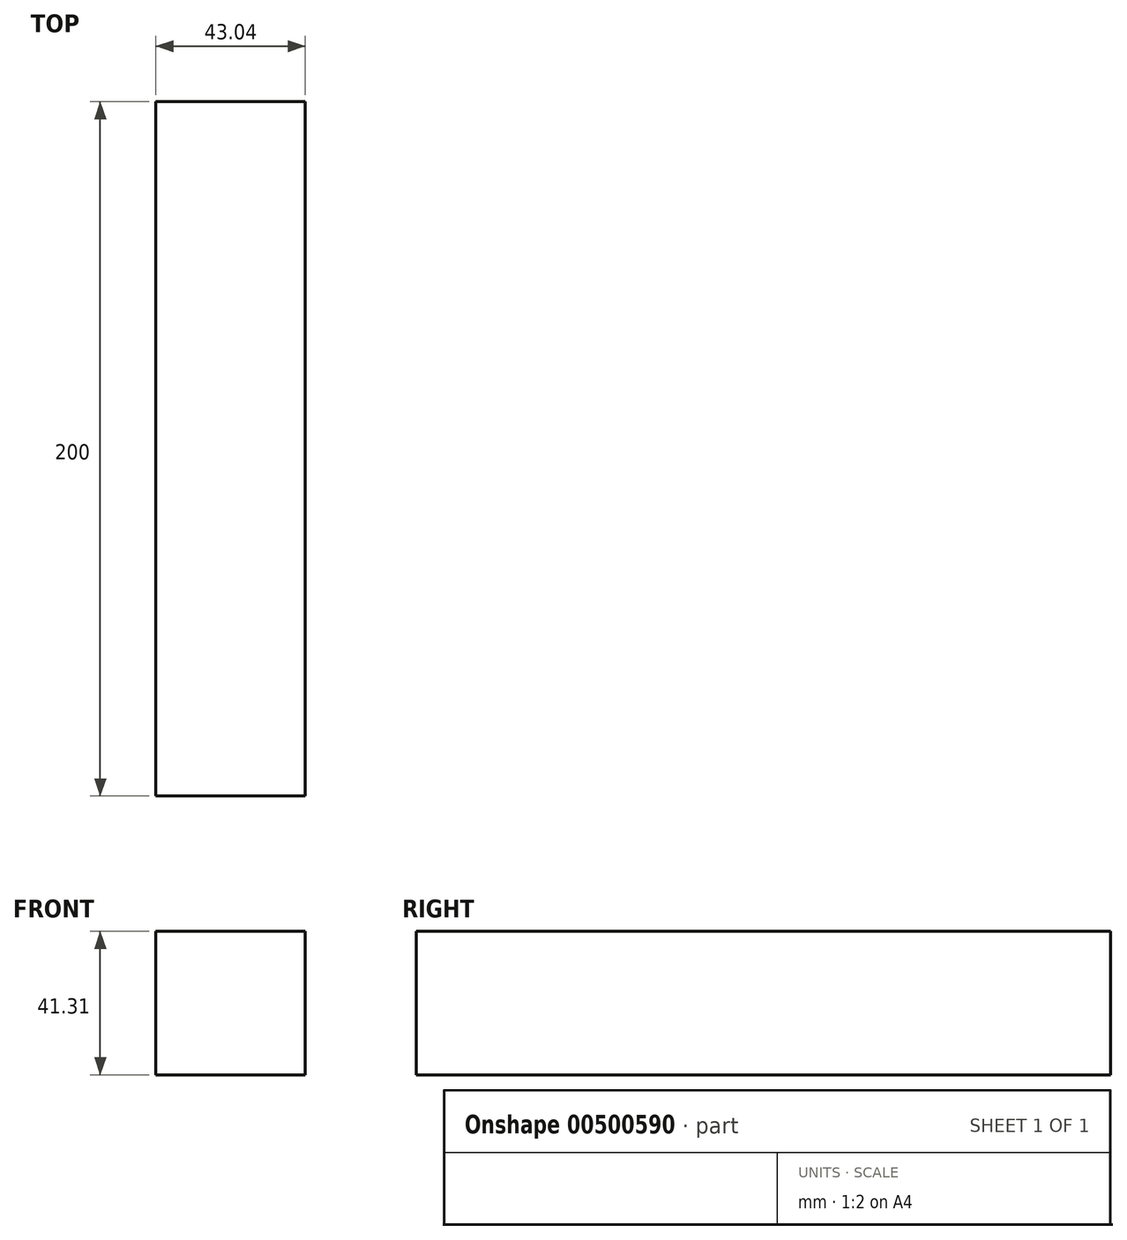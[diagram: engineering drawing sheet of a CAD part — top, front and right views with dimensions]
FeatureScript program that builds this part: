
annotation { "Feature Type Name" : "Feature", "Feature Type Description" : "" }
export const myFeature = defineFeature(function(context is Context, id is Id, definition is map)
    precondition{}
    {
        {
            var Q0;
            Q0=qCreatedBy(makeId("Front.planeOp"),FACE);
            var sketch = newSketch(context, id + "F0", { "sketchPlane" : qUnion([Q0])});
            skLineSegment(sketch, "E0.bottom", {"start": v(21.52, -23.38) * mm, "end": v(-21.52, -23.38) * mm});
            skLineSegment(sketch, "E0.top", {"start": v(21.52, 17.93) * mm, "end": v(-21.52, 17.93) * mm});
            skLineSegment(sketch, "E0.left", {"start": v(21.52, -23.38) * mm, "end": v(21.52, 17.93) * mm});
            skLineSegment(sketch, "E0.right", {"start": v(-21.52, -23.38) * mm, "end": v(-21.52, 17.93) * mm});
            skPoint(sketch, "E0.middle", {"position": v(0, -2.73) * mm});
            skSolve(sketch);
        }
        {
            var Q0;
            Q0=makeQuery(id+"F0.imprint","IMPRINT",FACE,{"disambiguationData":[TD([[makeQuery(id+"F0.imprint","IMPRINT",EDGE,{"derivedFrom":sQuery(id+"F0.wireOp",EDGE,"E0.bottom")}),-1.0]])]});
            extrude(context, id + "F1", {"entities" : qUnion([Q0]), "depth" : 200 * mm});
        }
    });
